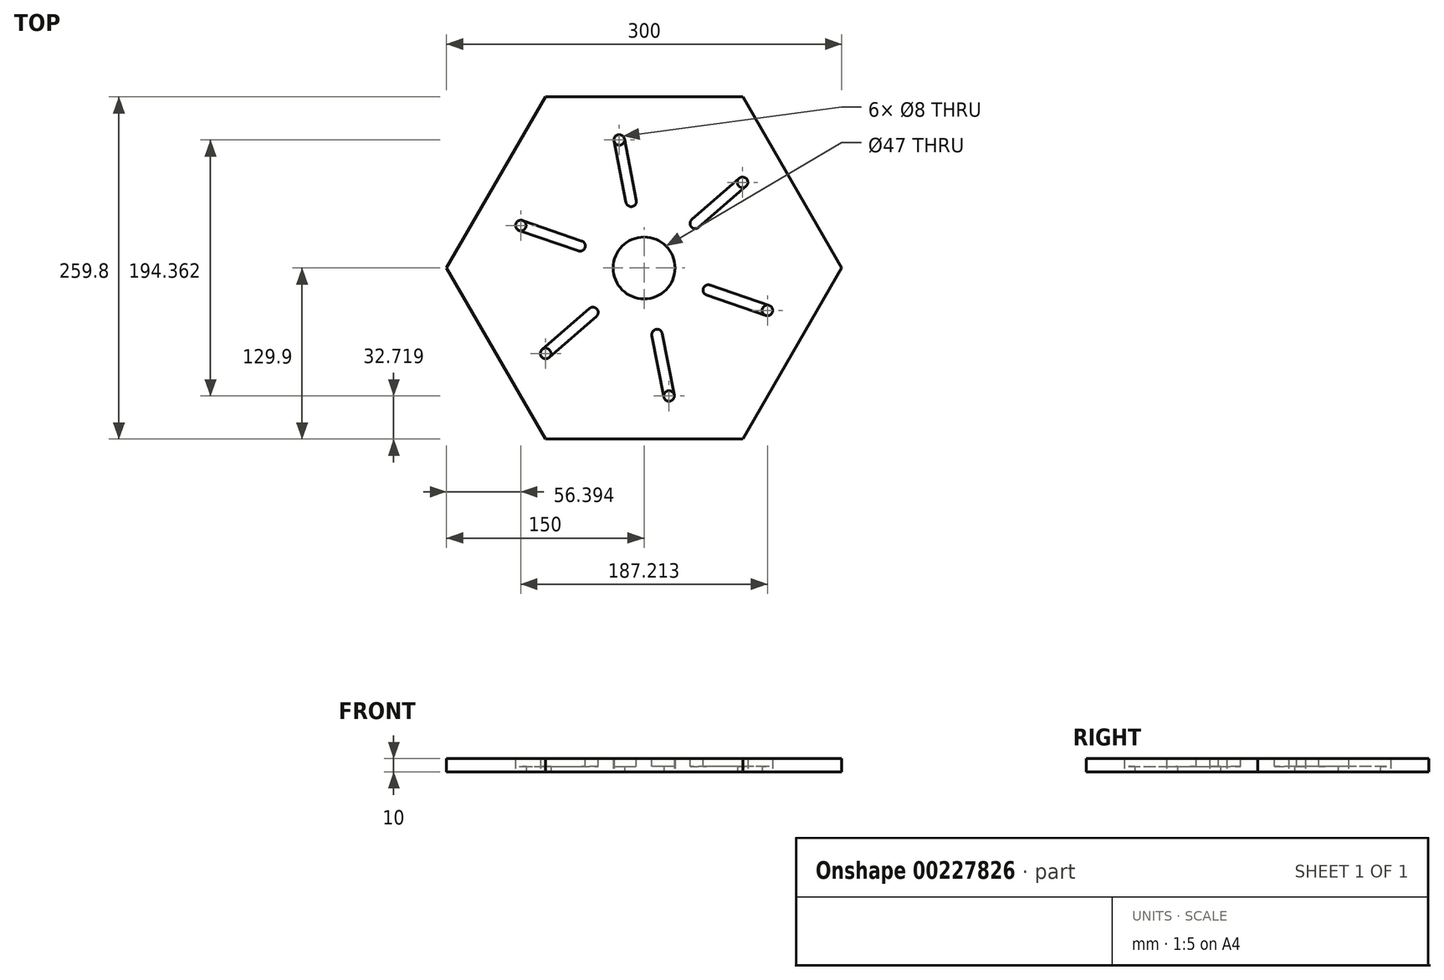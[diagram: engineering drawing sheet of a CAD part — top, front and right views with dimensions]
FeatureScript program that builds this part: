
annotation { "Feature Type Name" : "Feature", "Feature Type Description" : "" }
export const myFeature = defineFeature(function(context is Context, id is Id, definition is map)
    precondition{}
    {
        {
            var Q0;
            Q0=qCreatedBy(makeId("Top.planeOp"),FACE);
            var sketch = newSketch(context, id + "F0", { "sketchPlane" : qUnion([Q0])});
            skCircle(sketch, "E0.cCircle", {"center": v(0, 0) * mm, "radius": 150 * mm, "construction": true});
            skLineSegment(sketch, "E0.0", {"start": v(-150, 0) * mm, "end": v(-75, 129.9) * mm});
            skLineSegment(sketch, "E0.1", {"start": v(-75, 129.9) * mm, "end": v(75, 129.9) * mm});
            skLineSegment(sketch, "E0.2", {"start": v(75, 129.9) * mm, "end": v(150, 0) * mm});
            skLineSegment(sketch, "E0.3", {"start": v(150, 0) * mm, "end": v(75, -129.9) * mm});
            skLineSegment(sketch, "E0.4", {"start": v(75, -129.9) * mm, "end": v(-75, -129.9) * mm});
            skLineSegment(sketch, "E0.5", {"start": v(-75, -129.9) * mm, "end": v(-150, 0) * mm});
            skLineSegment(sketch, "E1", {"start": v(-125.66, 72.55) * mm, "end": v(0, 0) * mm, "construction": true});
            skLineSegment(sketch, "E2", {"start": v(-114.43, 89.16) * mm, "end": v(24.62, 8.88) * mm, "construction": true});
            skCircle(sketch, "E3", {"center": v(0, 0) * mm, "radius": 110 * mm, "construction": true});
            skLineSegment(sketch, "E4", {"start": v(-120.9, 10.58) * mm, "end": v(-58.23, 119.14) * mm, "construction": true});
            skCircle(sketch, "E5", {"center": v(0, 0) * mm, "radius": 95 * mm, "construction": true});
            skCircle(sketch, "E6", {"center": v(0, 0) * mm, "radius": 99 * mm, "construction": true});
            skLineSegment(sketch, "E7", {"start": v(-18.9, 97.18) * mm, "end": v(0, 0) * mm, "construction": true});
            skCircle(sketch, "E8", {"center": v(-18.9, 97.18) * mm, "radius": 4 * mm});
            skCircle(sketch, "E9", {"center": v(0, 0) * mm, "radius": 12 * mm});
            skCircle(sketch, "E10.1.0", {"center": v(-93.6, 32.23) * mm, "radius": 4 * mm});
            skCircle(sketch, "E10.2.0", {"center": v(-74.72, -64.95) * mm, "radius": 4 * mm});
            skCircle(sketch, "E10.3.0", {"center": v(18.9, -97.18) * mm, "radius": 4 * mm});
            skCircle(sketch, "E10.4.0", {"center": v(93.6, -32.23) * mm, "radius": 4 * mm});
            skCircle(sketch, "E10.5.0", {"center": v(74.72, 64.95) * mm, "radius": 4 * mm});
            skCircle(sketch, "E11", {"center": v(-85.26, 72.32) * mm, "radius": 65 * mm, "construction": true});
            skSolve(sketch);
        }
        {
            var Q0;
            Q0=makeQuery(id+"F0.imprint","IMPRINT",FACE,{"disambiguationData":[TD([[makeQuery(id+"F0.imprint","IMPRINT",EDGE,{"derivedFrom":sQuery(id+"F0.wireOp",EDGE,"E0.0")}),-1.0]])]});
            extrude(context, id + "F1", {"entities" : qUnion([Q0]), "depth" : 10 * mm});
        }
        {
            var Q0;
            Q0=makeQuery(id+"F0.imprint","IMPRINT",FACE,{"disambiguationData":[TD([[makeQuery(id+"F0.imprint","IMPRINT",EDGE,{"derivedFrom":sQuery(id+"F0.wireOp",EDGE,"E0.0")}),-1.0]])]});
            var sketch = newSketch(context, id + "F2", { "sketchPlane" : qUnion([Q0])});
            skCircle(sketch, "E12", {"center": v(0, 0) * mm, "radius": 23.5 * mm});
            skSolve(sketch);
        }
        {
            var Q0;
            Q0 = qSketchRegion(id + "F2", true);
            extrude(context, id + "F3", {"entities" : qUnion([Q0]), "operationType" : NewBodyOperationType.REMOVE, "depth" : 12 * mm});
        }
        {
            var Q0;
            Q0=makeQuery(id+"F1.opExtrude","CAP_FACE",FACE,{"disambiguationData":[OSD([sQuery(id+"F0.wireOp",EDGE,"E0.0"),sQuery(id+"F0.wireOp",EDGE,"E0.1"),sQuery(id+"F0.wireOp",EDGE,"E0.2"),sQuery(id+"F0.wireOp",EDGE,"E0.3"),sQuery(id+"F0.wireOp",EDGE,"E0.4"),sQuery(id+"F0.wireOp",EDGE,"E0.5"),sQuery(id+"F0.wireOp",EDGE,"E8"),sQuery(id+"F0.wireOp",EDGE,"E9"),sQuery(id+"F0.wireOp",EDGE,"E10.1.0"),sQuery(id+"F0.wireOp",EDGE,"E10.2.0"),sQuery(id+"F0.wireOp",EDGE,"E10.3.0"),sQuery(id+"F0.wireOp",EDGE,"E10.4.0"),sQuery(id+"F0.wireOp",EDGE,"E10.5.0")])],"isStart":false});
            var sketch = newSketch(context, id + "F4", { "sketchPlane" : qUnion([Q0])});
            skLineSegment(sketch, "E13.0", {"start": v(-150, 0) * mm, "end": v(-75, 129.9) * mm});
            skLineSegment(sketch, "E14.0", {"start": v(-22.36, 115.01) * mm, "end": v(0, 0) * mm, "construction": true});
            skArc(sketch, "E15", {"start": v(-14.96, 97.94) * mm, "mid": v(-19.65, 101.1) * mm, "end": v(-22.82, 96.42) * mm});
            skLineSegment(sketch, "E16", {"start": v(-22.82, 96.42) * mm, "end": v(-13.75, 49.8) * mm});
            skLineSegment(sketch, "E17.MirrorCS", {"start": v(-14.96, 97.94) * mm, "end": v(-5.9, 51.32) * mm});
            skArc(sketch, "E18", {"start": v(-13.75, 49.8) * mm, "mid": v(-9.06, 46.63) * mm, "end": v(-5.9, 51.32) * mm});
            skPoint(sketch, "E19.center", {"position": v(0, 0) * mm});
            skCircle(sketch, "E20", {"center": v(0, 0) * mm, "radius": 51.5 * mm, "construction": true});
            skCircle(sketch, "E21", {"center": v(0, 0) * mm, "radius": 99 * mm, "construction": true});
            skSolve(sketch);
        }
        {
            var Q0;
            Q0 = qSketchRegion(id + "F4", true);
            extrude(context, id + "F5", {"entities" : qUnion([Q0]), "oppositeDirection" : true, "depth" : 6 * mm, "hasSecondDirection" : true, "secondDirectionOppositeDirection" : false, "secondDirectionDepth" : 10 * mm});
        }
        {
            var Q0;
            Q0=makeQuery(id+"F5.opExtrude","SWEPT_BODY",BODY,{"disambiguationData":[OSD([sQuery(id+"F4.wireOp",EDGE,"E15"),sQuery(id+"F4.wireOp",EDGE,"E16"),sQuery(id+"F4.wireOp",EDGE,"E17.MirrorCS"),sQuery(id+"F4.wireOp",EDGE,"E18")])]});
            var Q1;
            Q1=makeQuery(id+"F3.boolean.opBoolean","COPY",FACE,{"derivedFrom":makeQuery(id+"F3.opExtrude","SWEPT_FACE",FACE,{"disambiguationData":[OSD([sQuery(id+"F2.wireOp",EDGE,"E12")])]})});
            circularPattern(context, id + "F6", {"operationType" : NewBodyOperationType.REMOVE, "entities" : qUnion([Q0]), "axis" : qUnion([Q1]), "angle" : 360 * degree, "instanceCount" : 6, "equalSpace" : true});
        }
    });
